# Revit family: LCV-WM
name_source: partatom
category: Lighting Fixtures
revit_build: Autodesk Revit 2013 (Build: 20130531_2115(x64)
units: mm (PartAtom-declared; Revit-internal decimal feet)

## types (6) — shared parameters
Assembly Code = D5020210
Color Filter = 16777215
Description = Curv LED Wall Mount
Dimming Lamp Color Temperature Shift = <None>
Emit Shape Visible in Rendering = No
Emit from Rectangle Length = 3 "
Emit from Rectangle Width = 48 "
Glass = Hubbell - White Glass
Housing Material = Hubbell - White
Housing Type = Perforated
Lamp = LED
Load Classification = Lighting
Manufacturer = Alera Lighting
Model = LCV-WM
Photometric Notes = More IES files download on Photometric Web Link
Photometric Web Link = https://www.hubbell.com
Power Factor = 1
Product Documentation Link = https://hubbellcdn.com
Product Page URL = https://www.hubbell.com
Row Option = LCV : 4'
Tilt Angle = 90.00°
URL = https://www.hubbell.com
Voltage = 120 V

## per-type parameters (varying)
| type | Apparent Load | LED Lumen Package | Photometric Web File | Watts |
| LCVWM-40LW-PERF | 40 VA | Low Watt | LCVWM-40LW-PERF.ies | 40 W |
| LCVWM-40HL-PERF | 50 VA | High Watt | LCVWM-40HL-PERF.ies | 50 W |
| LCVWM-35ML-PERF | 40 VA | Medium Watt | LCVWM-35ML-PERF.ies | 40 W |
| LCVWM-35LW-PERF | 30 VA | Low Watt | LCVWM-35LW-PERF.ies | 30 W |
| LCVWM-30ML-PERF | 40 VA | Medium Watt | LCVWM-30ML-PERF.ies | 40 W |
| LCVWM-30HL-PERF | 50 VA | High Watt | LCVWM-30HL-PERF.ies | 50 W |

## geometry (parser evidence)
native form markers: Sweep x4
no freeform markers — native parametric forms only
